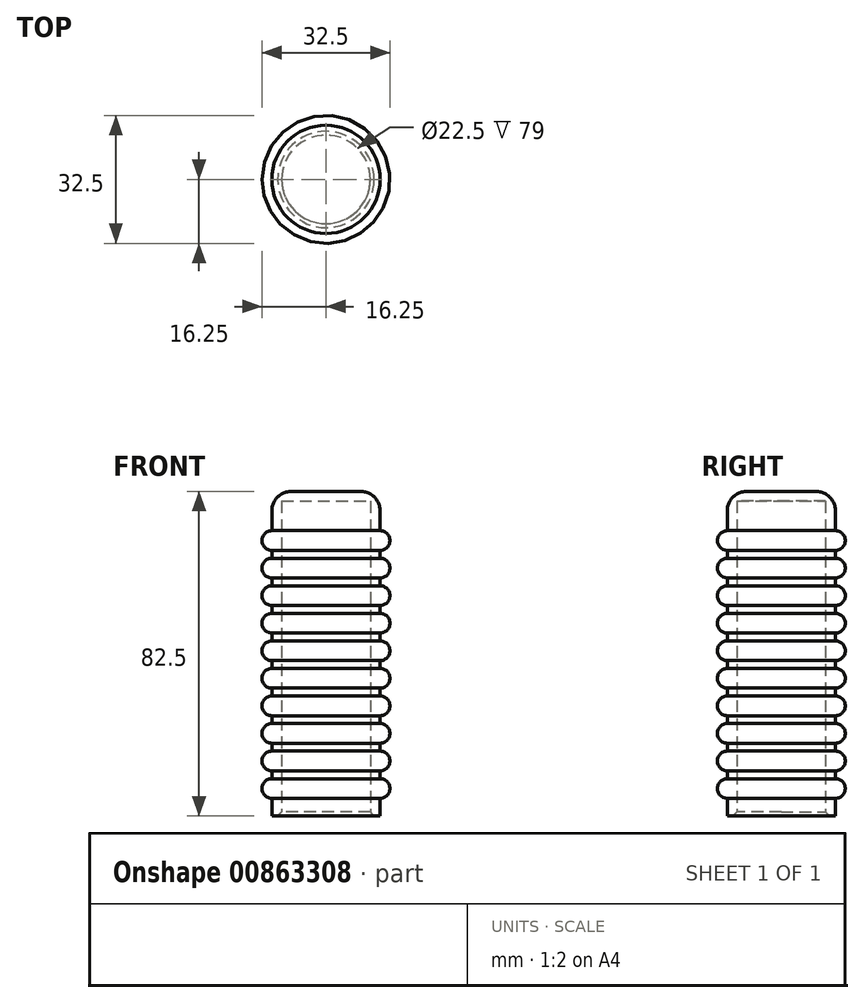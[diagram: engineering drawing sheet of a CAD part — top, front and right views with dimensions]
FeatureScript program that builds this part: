
annotation { "Feature Type Name" : "Feature", "Feature Type Description" : "" }
export const myFeature = defineFeature(function(context is Context, id is Id, definition is map)
    precondition{}
    {
        {
            var Q0;
            Q0=qCreatedBy(makeId("Front.planeOp"),FACE);
            var sketch = newSketch(context, id + "F0", { "sketchPlane" : qUnion([Q0])});
            skLineSegment(sketch, "E0", {"start": v(0, 0) * mm, "end": v(0, 82.5) * mm});
            skLineSegment(sketch, "E1", {"start": v(0, 82.5) * mm, "end": v(8.75, 82.5) * mm});
            skLineSegment(sketch, "E2", {"start": v(13.75, 77.5) * mm, "end": v(13.75, 0) * mm});
            skLineSegment(sketch, "E3", {"start": v(13.75, 0) * mm, "end": v(11.25, 0) * mm});
            skLineSegment(sketch, "E4", {"start": v(11.25, 0) * mm, "end": v(11.25, 80) * mm});
            skLineSegment(sketch, "E5", {"start": v(11.25, 80) * mm, "end": v(0, 80) * mm});
            skPoint(sketch, "E6.visualSharp", {"position": v(13.75, 82.5) * mm});
            skArc(sketch, "E6.filletArc", {"start": v(13.75, 77.5) * mm, "mid": v(12.29, 81.04) * mm, "end": v(8.75, 82.5) * mm});
            skArc(sketch, "E7", {"start": v(13.75, 4.5) * mm, "mid": v(16.25, 7) * mm, "end": v(13.75, 9.5) * mm});
            skArc(sketch, "E8.0.1.0", {"start": v(13.75, 11.5) * mm, "mid": v(16.25, 14) * mm, "end": v(13.75, 16.5) * mm});
            skArc(sketch, "E8.0.2.0", {"start": v(13.75, 18.5) * mm, "mid": v(16.25, 21) * mm, "end": v(13.75, 23.5) * mm});
            skArc(sketch, "E8.0.3.0", {"start": v(13.75, 25.5) * mm, "mid": v(16.25, 28) * mm, "end": v(13.75, 30.5) * mm});
            skArc(sketch, "E8.0.4.0", {"start": v(13.75, 32.5) * mm, "mid": v(16.25, 35) * mm, "end": v(13.75, 37.5) * mm});
            skArc(sketch, "E8.0.5.0", {"start": v(13.75, 39.5) * mm, "mid": v(16.25, 42) * mm, "end": v(13.75, 44.5) * mm});
            skArc(sketch, "E8.0.6.0", {"start": v(13.75, 46.5) * mm, "mid": v(16.25, 49) * mm, "end": v(13.75, 51.5) * mm});
            skArc(sketch, "E8.0.7.0", {"start": v(13.75, 53.5) * mm, "mid": v(16.25, 56) * mm, "end": v(13.75, 58.5) * mm});
            skArc(sketch, "E8.0.8.0", {"start": v(13.75, 60.5) * mm, "mid": v(16.25, 63) * mm, "end": v(13.75, 65.5) * mm});
            skArc(sketch, "E8.0.9.0", {"start": v(13.75, 67.5) * mm, "mid": v(16.25, 70) * mm, "end": v(13.75, 72.5) * mm});
            skLineSegment(sketch, "E8.direction1", {"start": v(13.75, 7) * mm, "end": v(38.75, 7) * mm, "construction": true});
            skLineSegment(sketch, "E8.direction2", {"start": v(13.75, 7) * mm, "end": v(13.75, 14) * mm, "construction": true});
            skSolve(sketch);
        }
        {
            var Q0;
            Q0=qSketchRegion(id+"F0",true);
            var Q1;
            Q1=sQuery(id+"F0.wireOp",EDGE,"E0");
            revolve(context, id + "F1", {"surfaceOperationType" : NewSurfaceOperationType.NEW, "entities" : qUnion([Q0]), "axis" : qUnion([Q1]), "revolveType" : RevolveType.FULL});
        }
        {
            var Q0;
            Q0=makeQuery(id+"F1.opRevolve","SWEPT_EDGE",EDGE,{"disambiguationData":[OSD([sQuery(id+"F0.wireOp",EDGE,"E3"),sQuery(id+"F0.wireOp",EDGE,"E4")])]});
            chamfer(context, id + "F2", {"entities" : qUnion([Q0]), "width" : 1 * mm, "tangentPropagation" : true});
        }
    });
